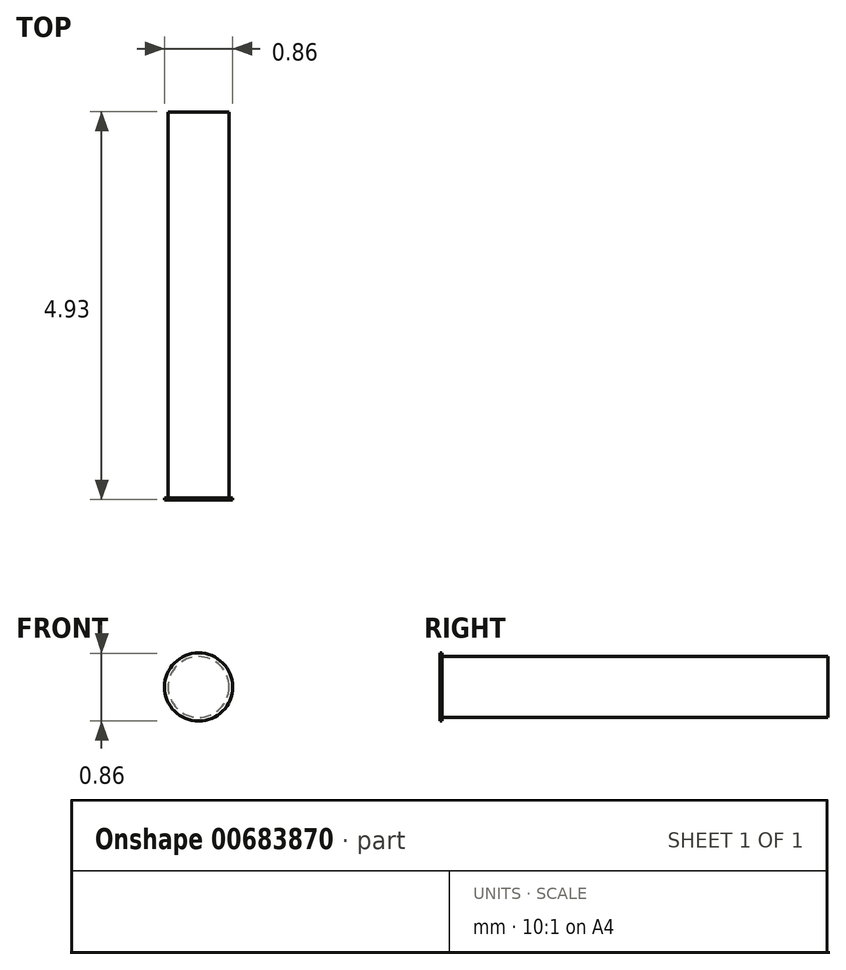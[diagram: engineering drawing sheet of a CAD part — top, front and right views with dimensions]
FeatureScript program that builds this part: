
annotation { "Feature Type Name" : "Feature", "Feature Type Description" : "" }
export const myFeature = defineFeature(function(context is Context, id is Id, definition is map)
    precondition{}
    {
        {
            var Q0;
            Q0=qCreatedBy(makeId("Front.planeOp"),FACE);
            var sketch = newSketch(context, id + "F0", { "sketchPlane" : qUnion([Q0])});
            skCircle(sketch, "E0", {"center": v(0, 0) * mm, "radius": 0.39 * mm});
            skSolve(sketch);
        }
        {
            var Q0;
            Q0 = qSketchRegion(id + "F0", true);
            extrude(context, id + "F1", {"entities" : qUnion([Q0]), "depth" : 0.46 * mm, "offsetDistance" : 25.4 * mm, "hasSecondDirection" : true, "secondDirectionOppositeDirection" : true, "secondDirectionDepth" : 4.44 * mm});
        }
        {
            var Q0;
            Q0=makeQuery(id+"F1.opExtrude","CAP_FACE",FACE,{"disambiguationData":[OSD([sQuery(id+"F0.wireOp",EDGE,"E0")])],"isStart":false});
            var sketch = newSketch(context, id + "F2", { "sketchPlane" : qUnion([Q0])});
            skCircle(sketch, "E1", {"center": v(0, 0) * mm, "radius": 0.43 * mm});
            skSolve(sketch);
        }
        {
            var Q0;
            Q0 = qSketchRegion(id + "F2", true);
            extrude(context, id + "F3", {"entities" : qUnion([Q0]), "operationType" : NewBodyOperationType.ADD, "depth" : 0.03 * mm, "offsetDistance" : 25.4 * mm});
        }
    });
